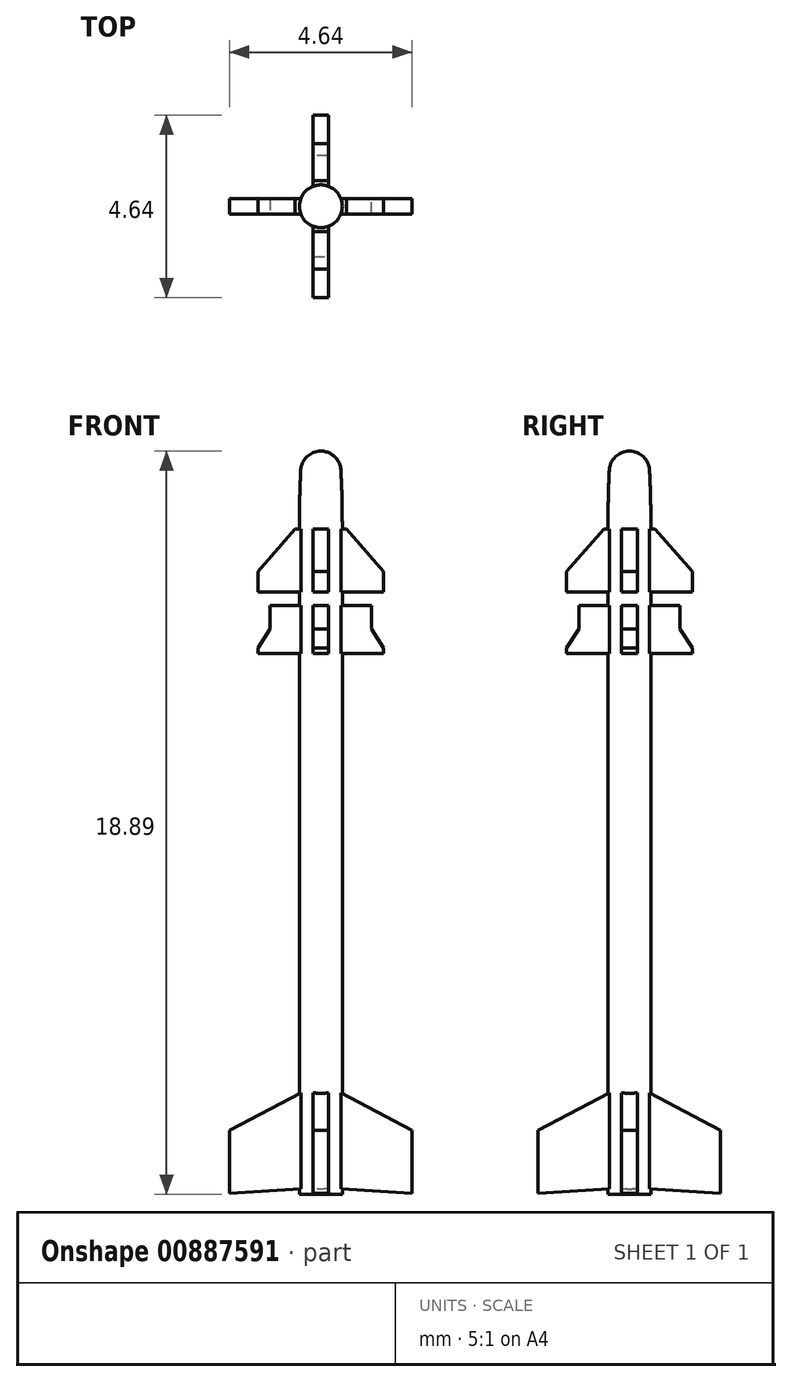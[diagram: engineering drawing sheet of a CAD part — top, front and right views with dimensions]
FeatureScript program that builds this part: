
annotation { "Feature Type Name" : "Feature", "Feature Type Description" : "" }
export const myFeature = defineFeature(function(context is Context, id is Id, definition is map)
    precondition{}
    {
        {
            var Q0;
            Q0=qCreatedBy(makeId("Front.planeOp"),FACE);
            var sketch = newSketch(context, id + "F0", { "sketchPlane" : qUnion([Q0])});
            skLineSegment(sketch, "E0", {"start": v(0, 0) * mm, "end": v(0, 18.89) * mm});
            skLineSegment(sketch, "E1", {"start": v(0.55, 17.01) * mm, "end": v(0.55, 0) * mm});
            skLineSegment(sketch, "E2", {"start": v(0.55, 0) * mm, "end": v(0, 0) * mm});
            skArc(sketch, "E3", {"start": v(0.51, 18.4) * mm, "mid": v(0.35, 18.75) * mm, "end": v(0, 18.89) * mm});
            skArc(sketch, "E4", {"start": v(0.55, 17.01) * mm, "mid": v(0.54, 17.7) * mm, "end": v(0.51, 18.4) * mm});
            skSolve(sketch);
        }
        {
            var Q0;
            {var subQ0=sQuery(id+"F0.wireOp",EDGE,"mrwio9nY-PsAZ-Zbfy-NhIU-sYq0QVbgGXAG");Q0=makeQuery(id+"F0.imprint","IMPRINT",FACE,{"disambiguationData":[TD([[makeQuery(id+"F0.imprint","IMPRINT",EDGE,{"derivedFrom":subQ0}),-1.0]])]});}
            var Q1;
            Q1=makeQuery(id+"F0.imprint","IMPRINT",FACE,{"disambiguationData":[TD([[makeQuery(id+"F0.imprint","IMPRINT",EDGE,{"derivedFrom":sQuery(id+"F0.wireOp",EDGE,"rEedh4zr-IGRr-Hqzj-sDLB-QnI7VE1V64O6.bottom")}),-1.0]])]});
            var Q2;
            Q2=makeQuery(id+"F0.imprint","IMPRINT",FACE,{"disambiguationData":[TD([[makeQuery(id+"F0.imprint","IMPRINT",EDGE,{"derivedFrom":sQuery(id+"F0.wireOp",EDGE,"E0")}),-1.0]])]});
            var Q3;
            Q3=makeQuery(id+"F0.imprint","IMPRINT",FACE,{"disambiguationData":[TD([[makeQuery(id+"F0.imprint","IMPRINT",EDGE,{"derivedFrom":sQuery(id+"F0.wireOp",EDGE,"p5wuz8j9-3HT4-kWwn-DjtP-lJmqTNSXSBJY.bottom")}),-1.0]])]});
            var Q4;
            Q4=sQuery(id+"F0.wireOp",EDGE,"E0");
            revolve(context, id + "F1", {"surfaceOperationType" : NewSurfaceOperationType.NEW, "entities" : qUnion([Q0, Q1, Q2, Q3]), "axis" : qUnion([Q4]), "revolveType" : RevolveType.FULL});
        }
        {
            var Q0;
            Q0=qCreatedBy(makeId("Front.planeOp"),FACE);
            var sketch = newSketch(context, id + "F2", { "sketchPlane" : qUnion([Q0])});
            skLineSegment(sketch, "E5", {"start": v(0, 0) * mm, "end": v(0, 16.9) * mm});
            skLineSegment(sketch, "E6", {"start": v(1.6, 13.75) * mm, "end": v(0.4, 13.75) * mm});
            skLineSegment(sketch, "E7", {"start": v(0.4, 13.75) * mm, "end": v(0.4, 2.65) * mm});
            skLineSegment(sketch, "E8", {"start": v(0.4, 2.65) * mm, "end": v(2.32, 1.63) * mm});
            skLineSegment(sketch, "E9", {"start": v(2.32, 1.63) * mm, "end": v(2.32, 0.03) * mm});
            skLineSegment(sketch, "E10", {"start": v(0.55, 0) * mm, "end": v(0.55, 32.87) * mm, "construction": true});
            skPoint(sketch, "E11", {"position": v(0.55, 2.57) * mm});
            skPoint(sketch, "E12", {"position": v(0.55, 13.75) * mm});
            skLineSegment(sketch, "E13", {"start": v(2.32, 0.03) * mm, "end": v(0, 0.17) * mm});
            skLineSegment(sketch, "E14.0", {"start": v(0.55, 0) * mm, "end": v(-0.55, 0) * mm});
            skPoint(sketch, "E15", {"position": v(0.55, 0.14) * mm});
            skLineSegment(sketch, "E16", {"start": v(1.6, 13.75) * mm, "end": v(1.6, 13.89) * mm});
            skLineSegment(sketch, "E17", {"start": v(1.6, 13.89) * mm, "end": v(1.28, 14.38) * mm});
            skLineSegment(sketch, "E18", {"start": v(1.28, 14.38) * mm, "end": v(1.28, 14.97) * mm});
            skLineSegment(sketch, "E19", {"start": v(1.28, 14.97) * mm, "end": v(0.4, 14.97) * mm});
            skLineSegment(sketch, "E20", {"start": v(0.4, 14.97) * mm, "end": v(0.4, 15.31) * mm});
            skLineSegment(sketch, "E21", {"start": v(0.4, 15.31) * mm, "end": v(1.6, 15.31) * mm});
            skLineSegment(sketch, "E22", {"start": v(1.6, 15.31) * mm, "end": v(1.6, 15.83) * mm});
            skLineSegment(sketch, "E23", {"start": v(1.6, 15.83) * mm, "end": v(0.65, 16.9) * mm});
            skLineSegment(sketch, "E24", {"start": v(0.65, 16.9) * mm, "end": v(0, 16.9) * mm});
            skSolve(sketch);
        }
        {
            var Q0;
            Q0=qSketchRegion(id+"F2",true);
            extrude(context, id + "F3", {"entities" : qUnion([Q0]), "operationType" : NewBodyOperationType.ADD, "depth" : .4 * mm, "offsetDistance" : 25 * mm, "symmetric" : true});
        }
        {
            var Q0;
            Q0=makeQuery(id+"F1.opRevolve","SWEPT_BODY",BODY,{"disambiguationData":[OSD([sQuery(id+"F0.wireOp",EDGE,"E0"),sQuery(id+"F0.wireOp",EDGE,"E1"),sQuery(id+"F0.wireOp",EDGE,"E2"),sQuery(id+"F0.wireOp",EDGE,"E3"),sQuery(id+"F0.wireOp",EDGE,"E4")])]});
            var Q1;
            Q1=makeQuery(id+"F1.opRevolve","SWEPT_FACE",FACE,{"disambiguationData":[OSD([sQuery(id+"F0.wireOp",EDGE,"E1")])]});
            circularPattern(context, id + "F4", {"operationType" : NewBodyOperationType.ADD, "entities" : qUnion([Q0]), "axis" : qUnion([Q1]), "angle" : 360 * degree, "instanceCount" : 4, "equalSpace" : true, "computeTransformsWithoutBuiltin" : true});
        }
    });
